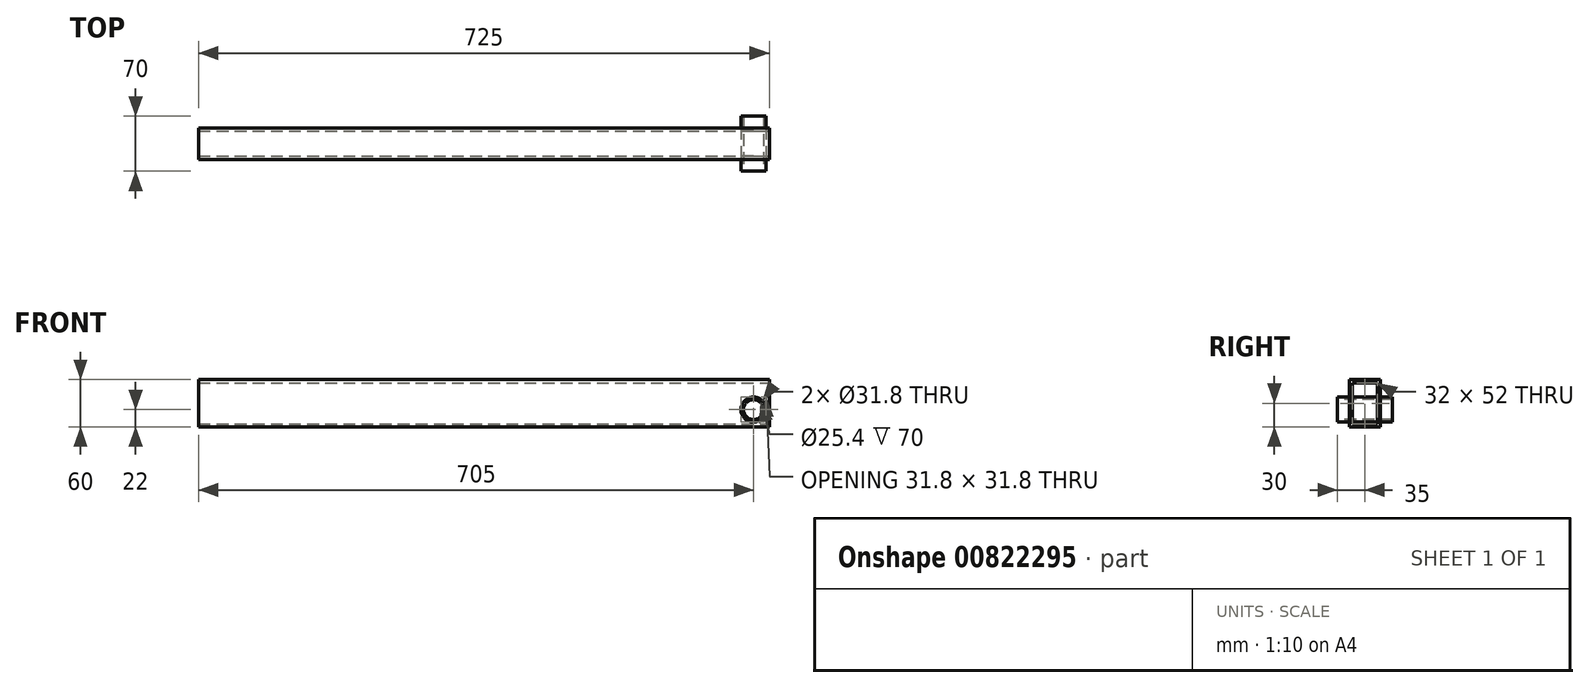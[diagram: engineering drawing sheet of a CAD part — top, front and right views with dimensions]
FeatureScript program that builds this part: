
annotation { "Feature Type Name" : "Feature", "Feature Type Description" : "" }
export const myFeature = defineFeature(function(context is Context, id is Id, definition is map)
    precondition{}
    {
        {
            var Q0;
            Q0=qCreatedBy(makeId("Right.planeOp"),FACE);
            var sketch = newSketch(context, id + "F0", { "sketchPlane" : qUnion([Q0])});
            skLineSegment(sketch, "E0.bottom", {"start": v(16, -26) * mm, "end": v(-16, -26) * mm});
            skLineSegment(sketch, "E0.top", {"start": v(16, 26) * mm, "end": v(-16, 26) * mm});
            skLineSegment(sketch, "E0.left", {"start": v(16, -26) * mm, "end": v(16, 26) * mm});
            skLineSegment(sketch, "E0.right", {"start": v(-16, -26) * mm, "end": v(-16, 26) * mm});
            skPoint(sketch, "E0.middle", {"position": v(0, 0) * mm});
            skLineSegment(sketch, "E1.bottom", {"start": v(20, -30) * mm, "end": v(-20, -30) * mm});
            skLineSegment(sketch, "E1.top", {"start": v(20, 30) * mm, "end": v(-20, 30) * mm});
            skLineSegment(sketch, "E1.left", {"start": v(20, -30) * mm, "end": v(20, 30) * mm});
            skLineSegment(sketch, "E1.right", {"start": v(-20, -30) * mm, "end": v(-20, 30) * mm});
            skSolve(sketch);
        }
        {
            var Q0;
            Q0 = qSketchRegion(id + "F0", true);
            extrude(context, id + "F1", {"entities" : qUnion([Q0]), "oppositeDirection" : true, "depth" : 725 * mm, "offsetDistance" : 25 * mm});
        }
        {
            var Q0;
            Q0=makeQuery(id+"F1.opExtrude","SWEPT_FACE",FACE,{"disambiguationData":[OSD([sQuery(id+"F0.wireOp",EDGE,"E1.right")])]});
            var sketch = newSketch(context, id + "F2", { "sketchPlane" : qUnion([Q0])});
            skLineSegment(sketch, "E2", {"start": v(0, 0) * mm, "end": v(0, -8) * mm});
            skLineSegment(sketch, "E3", {"start": v(0, -8) * mm, "end": v(-20, -8) * mm});
            skCircle(sketch, "E4", {"center": v(-20, -8) * mm, "radius": 15.9 * mm});
            skLineSegment(sketch, "E5", {"start": v(-20, -30) * mm, "end": v(-20, -26) * mm});
            skSolve(sketch);
        }
        {
            var Q0;
            Q0 = qSketchRegion(id + "F2", true);
            extrude(context, id + "F3", {"entities" : qUnion([Q0]), "operationType" : NewBodyOperationType.REMOVE, "oppositeDirection" : true, "depth" : 40 * mm, "offsetDistance" : 25 * mm});
        }
        {
            var Q0;
            Q0=makeQuery(id+"F1.opExtrude","SWEPT_FACE",FACE,{"disambiguationData":[OSD([sQuery(id+"F0.wireOp",EDGE,"E1.right")])]});
            var sketch = newSketch(context, id + "F4", { "sketchPlane" : qUnion([Q0])});
            skCircle(sketch, "E6", {"center": v(-20, -8) * mm, "radius": 15.88 * mm});
            skCircle(sketch, "E7", {"center": v(-20, -8) * mm, "radius": 12.7 * mm});
            skSolve(sketch);
        }
        {
            var Q0;
            Q0 = qSketchRegion(id + "F4", true);
            extrude(context, id + "F5", {"entities" : qUnion([Q0]), "oppositeDirection" : true, "depth" : 55 * mm, "offsetDistance" : 25 * mm});
        }
        {
            var Q0;
            Q0=makeQuery(id+"F5.opExtrude","CAP_FACE",FACE,{"disambiguationData":[OSD([sQuery(id+"F4.wireOp",EDGE,"E6"),sQuery(id+"F4.wireOp",EDGE,"E7")])],"isStart":true});
            extrude(context, id + "F6", {"entities" : qUnion([Q0]), "operationType" : NewBodyOperationType.ADD, "depth" : 15 * mm, "offsetDistance" : 25 * mm});
        }
    });
